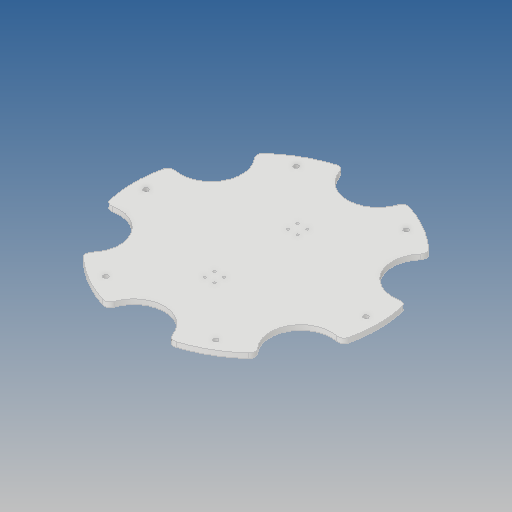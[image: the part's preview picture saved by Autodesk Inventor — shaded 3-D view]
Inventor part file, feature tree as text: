
AUTODESK INVENTOR PART (.ipt)
format: ipt  version: 2020 (Build 240168000, 168)  size: 211,968 bytes
history: native  units: mm
features: extrude x5, sketch x5, other x3, hole x3, pattern_circular x1, fillet x1
ambient origin geometry x8: Origin, YZ Plane, XZ Plane, XY Plane, X Axis, Y Axis, Z Axis, Center Point
bodies: Body1 (feature_tree)
feature tree (18):
  other  "крепление2"
  other  "Твердое тело1"
  extrude  "Выдавливание8"  Depth=4.0mm
  hole  "Отверстие2"  [1 undecoded]
  hole  "Отверстие3"  [1 undecoded]
  extrude  "Выдавливание9"  Depth=4.0mm
  pattern_circular  "Круговой массив1"  [2 undecoded]
  fillet  "Сопряжение1"  Radius=4.0mm
  extrude  "Выдавливание1"  Depth=4.0mm
  extrude  "Выдавливание4"  Depth=4.0mm
  extrude  "Выдавливание5"  Depth=9.0mm
  hole  "Отверстие1"  [1 undecoded]
  sketch  "Эскиз6"
  sketch  "Эскиз7"
  other  "Твердое тело2"
  sketch  "Эскиз8"
  sketch  "Эскиз9"
  sketch  "Эскиз10"
note: 5 required parameter values undecoded (feature->parameter linkage not recoverable at this tier; creation-order binding heuristic only, values carry confidence <= 0.55)
